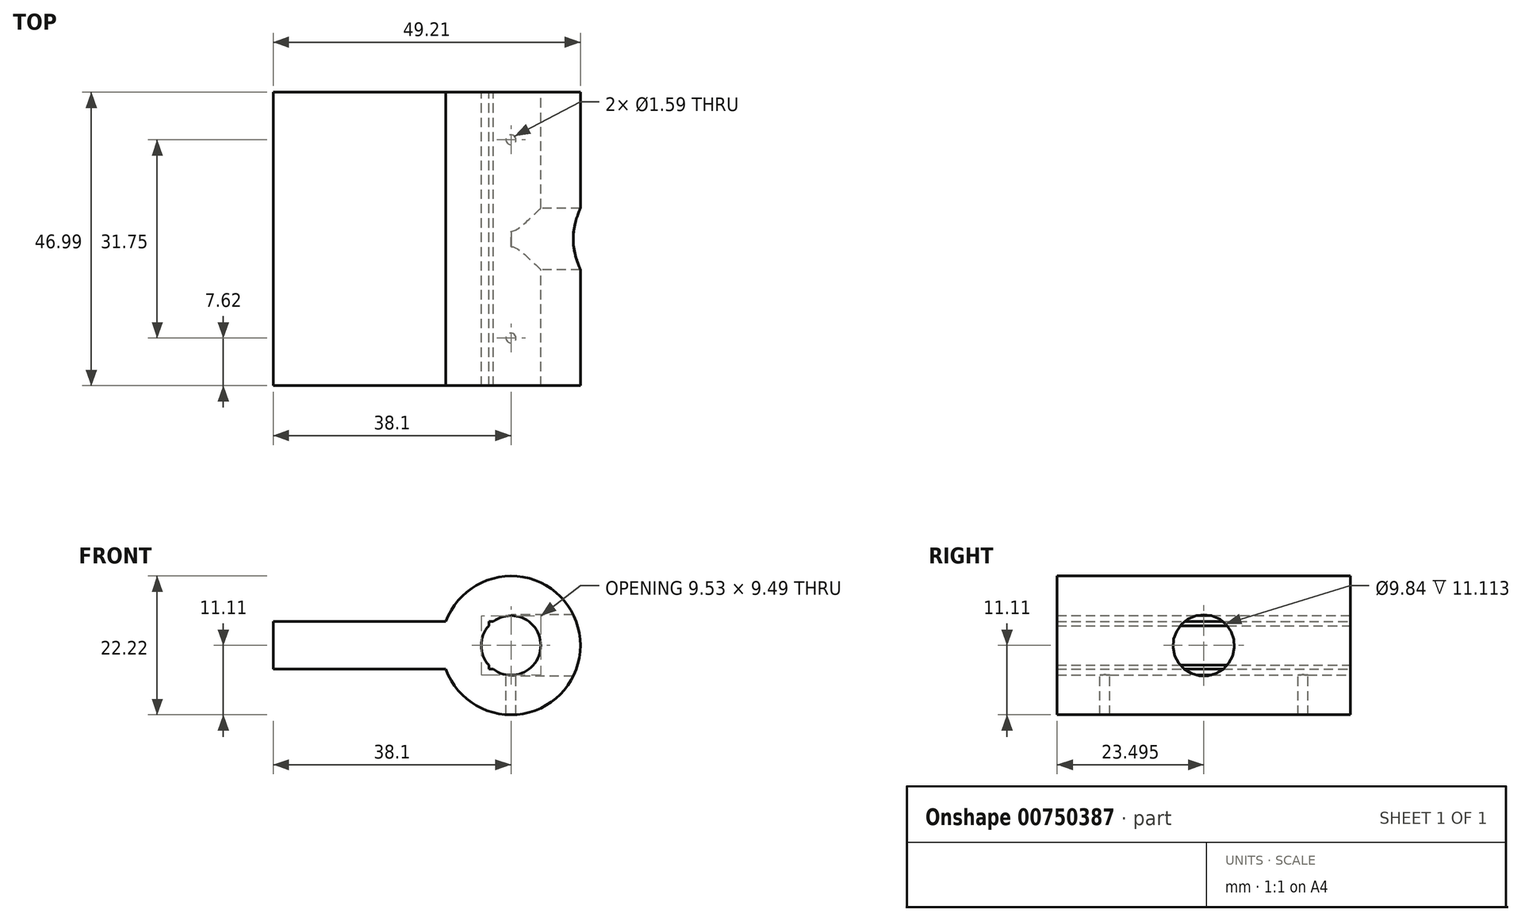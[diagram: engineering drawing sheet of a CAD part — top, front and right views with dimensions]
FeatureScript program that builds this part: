
annotation { "Feature Type Name" : "Feature", "Feature Type Description" : "" }
export const myFeature = defineFeature(function(context is Context, id is Id, definition is map)
    precondition{}
    {
        {
            var Q0;
            Q0=qCreatedBy(makeId("Front.planeOp"),FACE);
            var sketch = newSketch(context, id + "F0", { "sketchPlane" : qUnion([Q0])});
            skCircle(sketch, "E0", {"center": v(0, 0) * mm, "radius": 11.11 * mm});
            skCircle(sketch, "E1", {"center": v(0, 0) * mm, "radius": 4.76 * mm});
            skSolve(sketch);
        }
        {
            var Q0;
            Q0 = qSketchRegion(id + "F0", true);
            extrude(context, id + "F1", {"entities" : qUnion([Q0]), "depth" : 47 * mm, "offsetDistance" : 25.4 * mm});
        }
        {
            var Q0;
            Q0=qCreatedBy(makeId("Right.planeOp"),FACE);
            var sketch = newSketch(context, id + "F2", { "sketchPlane" : qUnion([Q0])});
            skLineSegment(sketch, "E2", {"start": v(0, -11.11) * mm, "end": v(-47, -11.11) * mm});
            skLineSegment(sketch, "E3", {"start": v(-47, 11.11) * mm, "end": v(0, 11.11) * mm});
            skLineSegment(sketch, "E4.0", {"start": v(-47, -11.11) * mm, "end": v(-47, 11.11) * mm});
            skLineSegment(sketch, "E5.bottom", {"start": v(0, -3.81) * mm, "end": v(-47, -3.81) * mm});
            skLineSegment(sketch, "E5.top", {"start": v(0, 3.81) * mm, "end": v(-47, 3.8) * mm});
            skLineSegment(sketch, "E5.left", {"start": v(0, -3.81) * mm, "end": v(0, 3.81) * mm});
            skLineSegment(sketch, "E5.right", {"start": v(-47, -3.81) * mm, "end": v(-47, 3.8) * mm});
            skSolve(sketch);
        }
        {
            var Q0;
            Q0 = qSketchRegion(id + "F2", true);
            extrude(context, id + "F3", {"entities" : qUnion([Q0]), "operationType" : NewBodyOperationType.ADD, "oppositeDirection" : true, "depth" : 38.1 * mm, "offsetDistance" : 25.4 * mm});
        }
        {
            var Q0;
            Q0=makeQuery(id+"F3.opExtrude","CAP_FACE",FACE,{"disambiguationData":[OSD([sQuery(id+"F2.wireOp",EDGE,"E5.bottom"),sQuery(id+"F2.wireOp",EDGE,"E5.top"),sQuery(id+"F2.wireOp",EDGE,"E5.left"),sQuery(id+"F2.wireOp",EDGE,"E5.right")])],"isStart":true});
            extrude(context, id + "F4", {"entities" : qUnion([Q0]), "operationType" : NewBodyOperationType.REMOVE, "oppositeDirection" : true, "depth" : 3.56 * mm, "offsetDistance" : 25.4 * mm});
        }
        {
            var Q0;
            Q0=qCreatedBy(makeId("Top.planeOp"),FACE);
            var sketch = newSketch(context, id + "F5", { "sketchPlane" : qUnion([Q0])});
            skLineSegment(sketch, "E6", {"start": v(11.11, 0) * mm, "end": v(11.11, -47) * mm});
            skCircle(sketch, "E7", {"center": v(0, -7.62) * mm, "radius": 0.8 * mm});
            skCircle(sketch, "E8", {"center": v(0, -39.37) * mm, "radius": 0.8 * mm});
            skSolve(sketch);
        }
        {
            var Q0;
            Q0 = qSketchRegion(id + "F5", true);
            extrude(context, id + "F6", {"entities" : qUnion([Q0]), "operationType" : NewBodyOperationType.REMOVE, "oppositeDirection" : true, "depth" : 25.4 * mm, "offsetDistance" : 25.4 * mm});
        }
        {
            var Q0;
            Q0=qCreatedBy(makeId("Right.planeOp"),FACE);
            var sketch = newSketch(context, id + "F7", { "sketchPlane" : qUnion([Q0])});
            skLineSegment(sketch, "E9", {"start": v(0, -11.11) * mm, "end": v(-47, -11.11) * mm});
            skLineSegment(sketch, "E10", {"start": v(-47, 11.11) * mm, "end": v(0, 11.11) * mm});
            skCircle(sketch, "E11", {"center": v(-23.5, 0) * mm, "radius": 4.92 * mm});
            skSolve(sketch);
        }
        {
            var Q0;
            Q0 = qSketchRegion(id + "F7", true);
            extrude(context, id + "F8", {"entities" : qUnion([Q0]), "operationType" : NewBodyOperationType.REMOVE, "depth" : 25.4 * mm, "offsetDistance" : 25.4 * mm});
        }
        {
            var Q0;
            Q0=makeQuery(id+"F3.boolean.opBoolean","MERGE",FACE,{"derivedFrom":[makeQuery(id+"F1.opExtrude","CAP_FACE",FACE,{"disambiguationData":[OSD([sQuery(id+"F0.wireOp",EDGE,"E0"),sQuery(id+"F0.wireOp",EDGE,"E1")])],"isStart":true}),makeQuery(id+"F3.opExtrude","SWEPT_FACE",FACE,{"disambiguationData":[OSD([sQuery(id+"F2.wireOp",EDGE,"E5.left")])]})]});
            var sketch = newSketch(context, id + "F9", { "sketchPlane" : qUnion([Q0])});
            skArc(sketch, "E12.0", {"start": v(10.44, -3.81) * mm, "mid": v(-11.11, 0) * mm, "end": v(10.44, 3.81) * mm});
            skArc(sketch, "E13.0", {"start": v(2.86, -3.81) * mm, "mid": v(-4.76, 0) * mm, "end": v(2.86, 3.81) * mm});
            skCircle(sketch, "E14", {"center": v(0, 0) * mm, "radius": 4.76 * mm});
            skSolve(sketch);
        }
        {
            var Q0;
            Q0 = qSketchRegion(id + "F9", true);
            extrude(context, id + "F10", {"entities" : qUnion([Q0]), "operationType" : NewBodyOperationType.REMOVE, "endBound" : BoundingType.THROUGH_ALL, "oppositeDirection" : true, "depth" : 25.4 * mm, "offsetDistance" : 25.4 * mm});
        }
    });
